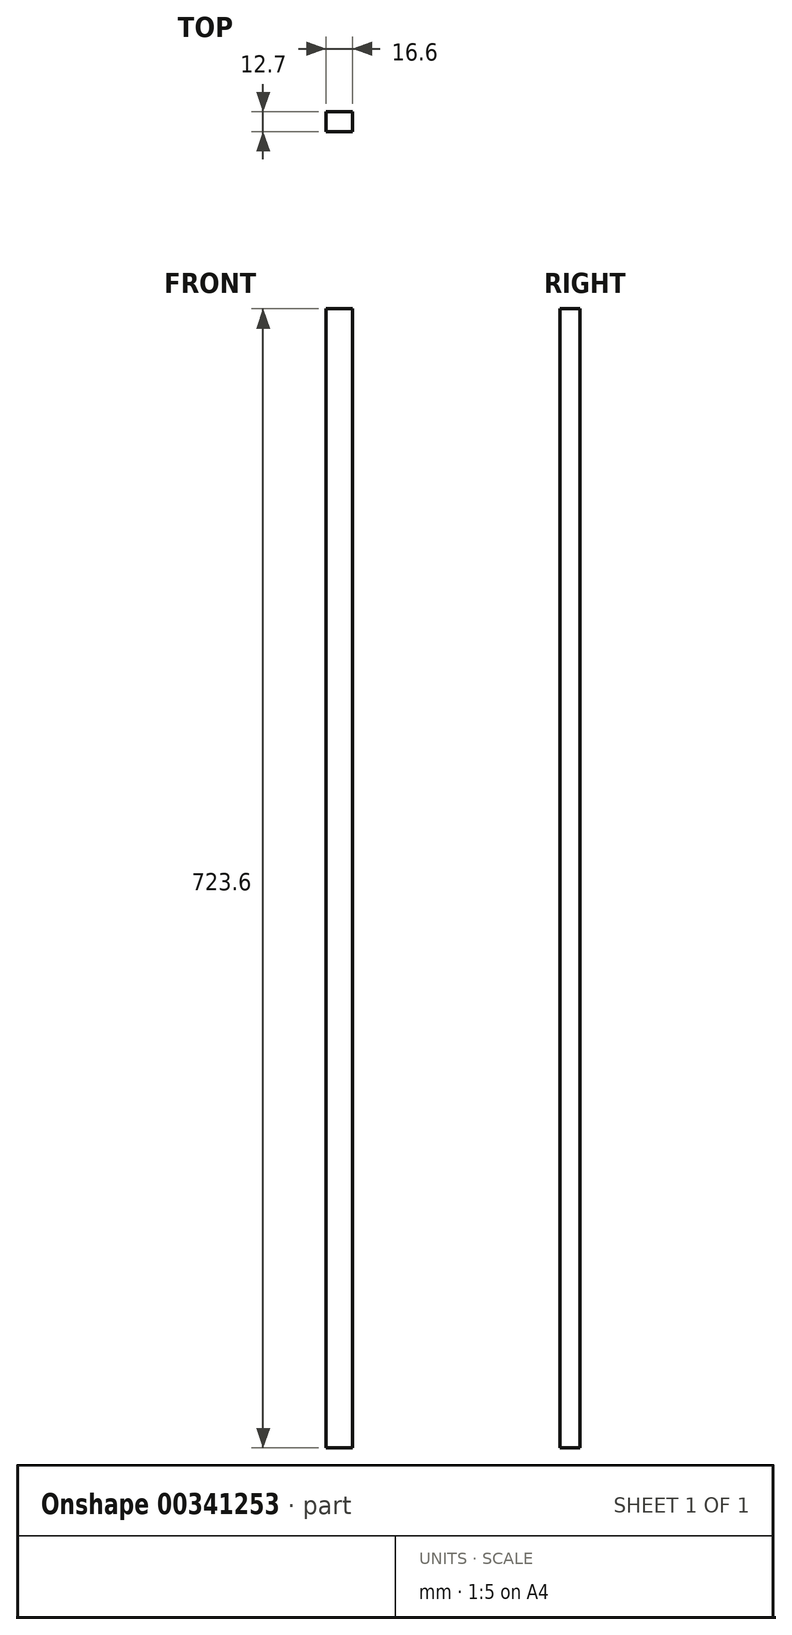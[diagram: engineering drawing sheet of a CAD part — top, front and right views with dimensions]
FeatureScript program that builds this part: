
annotation { "Feature Type Name" : "Feature", "Feature Type Description" : "" }
export const myFeature = defineFeature(function(context is Context, id is Id, definition is map)
    precondition{}
    {
        {
            var Q0;
            Q0=qCreatedBy(makeId("Front.planeOp"),FACE);
            var sketch = newSketch(context, id + "F0", { "sketchPlane" : qUnion([Q0])});
            skLineSegment(sketch, "E0.bottom", {"start": v(-8.3, 361.8) * mm, "end": v(8.3, 361.8) * mm});
            skLineSegment(sketch, "E0.top", {"start": v(-8.3, -361.8) * mm, "end": v(8.3, -361.8) * mm});
            skLineSegment(sketch, "E0.left", {"start": v(-8.3, 361.8) * mm, "end": v(-8.3, -361.8) * mm});
            skLineSegment(sketch, "E0.right", {"start": v(8.3, 361.8) * mm, "end": v(8.3, -361.8) * mm});
            skPoint(sketch, "E0.middle", {"position": v(0, 0) * mm});
            skSolve(sketch);
        }
        {
            var Q0;
            Q0=makeQuery(id+"F0.imprint","IMPRINT",FACE,{"disambiguationData":[TD([[makeQuery(id+"F0.imprint","IMPRINT",EDGE,{"derivedFrom":sQuery(id+"F0.wireOp",EDGE,"E0.bottom")}),-1.0]])]});
            extrude(context, id + "F1", {"entities" : qUnion([Q0]), "depth" : 12.7 * mm});
        }
    });
